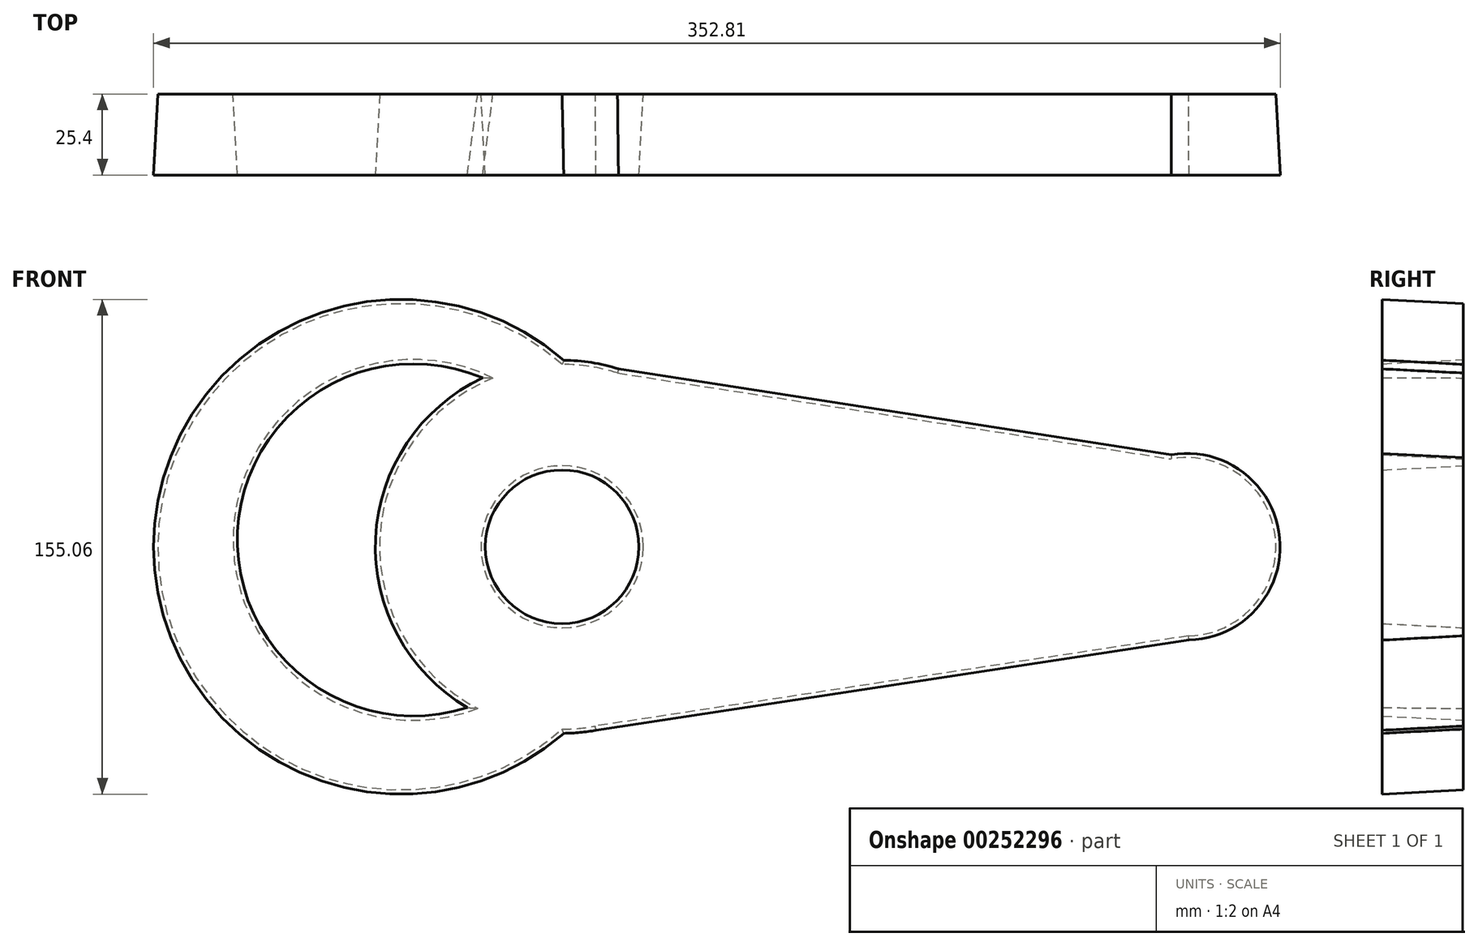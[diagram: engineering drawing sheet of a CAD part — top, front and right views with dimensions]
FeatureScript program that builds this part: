
annotation { "Feature Type Name" : "Feature", "Feature Type Description" : "" }
export const myFeature = defineFeature(function(context is Context, id is Id, definition is map)
    precondition{}
    {
        {
            var Q0;
            Q0=qCreatedBy(makeId("Front.planeOp"),FACE);
            var sketch = newSketch(context, id + "F0", { "sketchPlane" : qUnion([Q0])});
            skCircle(sketch, "E0", {"center": v(0, 0) * mm, "radius": 57.15 * mm});
            skCircle(sketch, "E1", {"center": v(195.61, 0) * mm, "radius": 27.94 * mm});
            skLineSegment(sketch, "E2", {"start": v(0, 57.15) * mm, "end": v(190.75, 27.51) * mm});
            skCircle(sketch, "E3", {"center": v(0, 0) * mm, "radius": 25.4 * mm});
            skArc(sketch, "E4", {"start": v(0, 57.15) * mm, "mid": v(-126.6, 0) * mm, "end": v(0, -57.15) * mm});
            skArc(sketch, "E5", {"start": v(-21.63, 52.9) * mm, "mid": v(-102.98, 4.77) * mm, "end": v(-26.43, -50.67) * mm});
            skLineSegment(sketch, "E6", {"start": v(10.4, -56.2) * mm, "end": v(203.34, -26.85) * mm});
            skSolve(sketch);
        }
        {
            var Q0;
            Q0 = qSketchRegion(id + "F0", true);
            extrude(context, id + "F1", {"entities" : qUnion([Q0]), "depth" : 25.4 * mm, "hasDraft" : true, "draftAngle" : 3 * degree});
        }
        {
            var Q0;
            Q0 = qSketchRegion(id + "F0", true);
            extrude(context, id + "F2", {"entities" : qUnion([Q0]), "operationType" : NewBodyOperationType.ADD, "depth" : 25.4 * mm});
        }
        {
            var Q0;
            Q0 = qSketchRegion(id + "F0", true);
            extrude(context, id + "F3", {"entities" : qUnion([Q0]), "operationType" : NewBodyOperationType.ADD, "depth" : 25.4 * mm});
        }
    });
